# Revit family: LCC8LED-Pendant
name_source: partatom
category: Lighting Fixtures
revit_build: Autodesk Revit Architecture 2012 (Build: 20110309_2315(x64)
units: mm (PartAtom-declared; Revit-internal decimal feet)

## types (5) — shared parameters
Apparent Load = 0 VA
Default Elevation = 48.000"
Description = 8in LED Pendant Mount Cylinder
Glass = Hubbell - White Glass
Lamp = LED Lamp
Load Classification = Lighting
Manufacturer = Prescolite
Manufacturer Fax = 866-898-0131
Model = LCC8LED
URL = http://www.prescolite.com
Voltage = 120 V

## per-type parameters (varying)
| type | Backbox | Length | Photometric Web |
| LCC8LED-Matte White | Hubbell - Matt White | 34.875" | Web LCC8LED : LCC8LEDS10L30K8WFL45 |
| LCC8LED-Matte Black | Hubbell - Matte Black | 36.000" | Web LCC8LED : LCC8LEDS18L30K8WFL45 |
| LCC8LED-Bronze | Hubbell - Bronze | 34.875" | Web LCC8LED : LCC8LEDS10L30K8WFL45 |
| LCC8LED-Brushed Aluminium | Hubbell - Brushed Aluminum | 34.875" | Web LCC8LED : LCC8LEDS10L30K8WFL45 |
| LCC8LED-Zet | Hubbell - Zet | 34.875" | Web LCC8LED : LCC8LEDS10L30K8WFL45 |

## geometry (parser evidence)
native form markers: Blend x10, Sweep x7
no freeform markers — native parametric forms only
